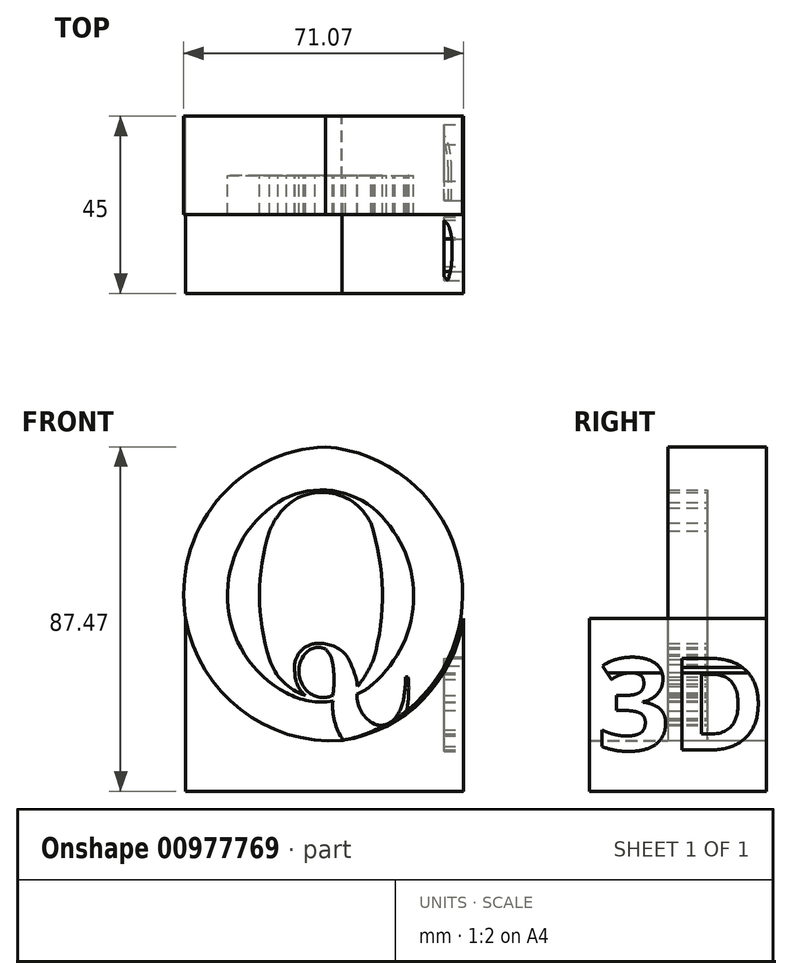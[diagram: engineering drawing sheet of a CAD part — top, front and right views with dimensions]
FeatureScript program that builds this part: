
annotation { "Feature Type Name" : "Feature", "Feature Type Description" : "" }
export const myFeature = defineFeature(function(context is Context, id is Id, definition is map)
    precondition{}
    {
        {
            var Q0;
            Q0=qCreatedBy(makeId("Front.planeOp"),FACE);
            var sketch = newSketch(context, id + "F0", { "sketchPlane" : qUnion([Q0])});
            skPoint(sketch, "E0.first.point", {"position": v(-8.97, 42.4) * mm});
            skPoint(sketch, "E0.second.point", {"position": v(4.84, -31.38) * mm});
            skPoint(sketch, "E0.third.point", {"position": v(40.23, 13.72) * mm});
            skArc(sketch, "E1", {"start": v(0, 43.7) * mm, "mid": v(-36.34, 3.66) * mm, "end": v(4.84, -31.38) * mm});
            skArc(sketch, "E2", {"start": v(20.57, -24) * mm, "mid": v(33.91, 17.02) * mm, "end": v(0, 43.7) * mm});
            skArc(sketch, "E3", {"start": v(-12, 29.47) * mm, "mid": v(-24.84, 4.65) * mm, "end": v(-9.87, -18.96) * mm});
            skArc(sketch, "E4", {"start": v(12.09, 28.05) * mm, "mid": v(0.27, 32.56) * mm, "end": v(-12, 29.47) * mm});
            skArc(sketch, "E5", {"start": v(12.09, -16.68) * mm, "mid": v(22.4, 5.68) * mm, "end": v(12.09, 28.05) * mm});
            skArc(sketch, "E6", {"start": v(8.11, -19.25) * mm, "mid": v(10.22, -18.15) * mm, "end": v(12.09, -16.68) * mm});
            skArc(sketch, "E7", {"start": v(-9.87, -18.96) * mm, "mid": v(-4.16, -21) * mm, "end": v(1.9, -21.05) * mm});
            skArc(sketch, "E8", {"start": v(1.9, -21.05) * mm, "mid": v(2.44, -26.48) * mm, "end": v(4.84, -31.38) * mm});
            skArc(sketch, "E9", {"start": v(8.11, -19.25) * mm, "mid": v(9.16, -23.77) * mm, "end": v(12.57, -26.92) * mm});
            skArc(sketch, "E10", {"start": v(12.57, -26.92) * mm, "mid": v(15.38, -27) * mm, "end": v(17.7, -25.42) * mm});
            skArc(sketch, "E11", {"start": v(17.7, -25.42) * mm, "mid": v(19.27, -22.75) * mm, "end": v(19.99, -19.74) * mm});
            skArc(sketch, "E12", {"start": v(19.99, -19.74) * mm, "mid": v(20.3, -17.3) * mm, "end": v(20.33, -14.85) * mm});
            skLineSegment(sketch, "E13", {"start": v(20.33, -14.85) * mm, "end": v(21.05, -14.85) * mm});
            skArc(sketch, "E14", {"start": v(20.57, -24) * mm, "mid": v(21.16, -19.45) * mm, "end": v(21.05, -14.85) * mm});
            skArc(sketch, "E15", {"start": v(11.56, 24.17) * mm, "mid": v(0.05, 31.98) * mm, "end": v(-12.33, 25.65) * mm});
            skArc(sketch, "E16", {"start": v(-12.33, 25.65) * mm, "mid": v(-13.33, 23.93) * mm, "end": v(-14.2, 22.14) * mm});
            skArc(sketch, "E17", {"start": v(12.27, -10.4) * mm, "mid": v(14.51, 6.94) * mm, "end": v(11.56, 24.17) * mm});
            skArc(sketch, "E18", {"start": v(8.2, -17.28) * mm, "mid": v(10.48, -13.99) * mm, "end": v(12.27, -10.4) * mm});
            skArc(sketch, "E19", {"start": v(-14.2, 22.14) * mm, "mid": v(-16.74, 5.87) * mm, "end": v(-14.2, -10.4) * mm});
            skArc(sketch, "E20", {"start": v(-14.2, -10.4) * mm, "mid": v(-10.74, -16.1) * mm, "end": v(-5.08, -19.62) * mm});
            skArc(sketch, "E21.trimOffspring", {"start": v(21.12, -15.68) * mm, "mid": v(21.07, -15.26) * mm, "end": v(21.03, -14.85) * mm});
            skArc(sketch, "E22", {"start": v(-7.75, -13.7) * mm, "mid": v(-7.09, -16.96) * mm, "end": v(-5.08, -19.62) * mm});
            skArc(sketch, "E23", {"start": v(-2.67, -6.43) * mm, "mid": v(-6.77, -8.98) * mm, "end": v(-7.75, -13.7) * mm});
            skArc(sketch, "E24", {"start": v(5.17, -9.2) * mm, "mid": v(1.57, -6.89) * mm, "end": v(-2.67, -6.43) * mm});
            skArc(sketch, "E25", {"start": v(8.2, -17.28) * mm, "mid": v(7.13, -13.07) * mm, "end": v(5.17, -9.2) * mm});
            skArc(sketch, "E26", {"start": v(1.9, -19.62) * mm, "mid": v(2.22, -15.67) * mm, "end": v(1.9, -11.72) * mm});
            skArc(sketch, "E27", {"start": v(1.9, -11.72) * mm, "mid": v(1.3, -9.59) * mm, "end": v(0, -7.8) * mm});
            skArc(sketch, "E28", {"start": v(0, -7.8) * mm, "mid": v(-3.12, -7.64) * mm, "end": v(-5.56, -9.59) * mm});
            skPoint(sketch, "E28.endSnap0", {"position": v(1.3, -9.59) * mm});
            skArc(sketch, "E29", {"start": v(-5.56, -9.59) * mm, "mid": v(-6.65, -14.33) * mm, "end": v(-4.4, -18.65) * mm});
            skArc(sketch, "E30", {"start": v(-4.4, -18.65) * mm, "mid": v(-1.39, -20.08) * mm, "end": v(1.9, -19.62) * mm});
            skSolve(sketch);
        }
        {
            var Q0;
            Q0=qSketchRegion(id+"F0",true);
            extrude(context, id + "F1", {"entities" : qUnion([Q0]), "depth" : 25 * mm, "offsetDistance" : 25 * mm});
        }
        {
            var Q0;
            Q0=makeQuery(id+"F1.opExtrude","CAP_FACE",FACE,{"disambiguationData":[OSD([sQuery(id+"F0.wireOp",EDGE,"E1"),sQuery(id+"F0.wireOp",EDGE,"E2"),sQuery(id+"F0.wireOp",EDGE,"E3"),sQuery(id+"F0.wireOp",EDGE,"E4"),sQuery(id+"F0.wireOp",EDGE,"E5"),sQuery(id+"F0.wireOp",EDGE,"E6"),sQuery(id+"F0.wireOp",EDGE,"E7"),sQuery(id+"F0.wireOp",EDGE,"E8"),sQuery(id+"F0.wireOp",EDGE,"E9"),sQuery(id+"F0.wireOp",EDGE,"E10"),sQuery(id+"F0.wireOp",EDGE,"E11"),sQuery(id+"F0.wireOp",EDGE,"E12"),sQuery(id+"F0.wireOp",EDGE,"E13"),sQuery(id+"F0.wireOp",EDGE,"E14"),sQuery(id+"F0.wireOp",EDGE,"E21.trimOffspring")])],"isStart":true});
            var sketch = newSketch(context, id + "F2", { "sketchPlane" : qUnion([Q0])});
            skArc(sketch, "E31", {"start": v(0, 43.7) * mm, "mid": v(-35.47, 8.29) * mm, "end": v(-4.84, -31.38) * mm});
            skArc(sketch, "E32", {"start": v(-4.84, -31.38) * mm, "mid": v(36.41, 3.65) * mm, "end": v(0, 43.7) * mm});
            skSolve(sketch);
        }
        {
            var Q0;
            Q0=qCreatedBy(makeId("Front.planeOp"),FACE);
            var sketch = newSketch(context, id + "F3", { "sketchPlane" : qUnion([Q0])});
            skArc(sketch, "E33", {"start": v(0, 43.75) * mm, "mid": v(-36.28, 3.67) * mm, "end": v(4.78, -31.5) * mm});
            skArc(sketch, "E34", {"start": v(4.78, -31.5) * mm, "mid": v(35.24, 8.21) * mm, "end": v(0, 43.75) * mm});
            skSolve(sketch);
        }
        {
            var Q0;
            Q0=qSketchRegion(id+"F3",true);
            extrude(context, id + "F4", {"entities" : qUnion([Q0]), "operationType" : NewBodyOperationType.ADD, "depth" : 10 * mm, "offsetDistance" : 25 * mm});
        }
        {
            var Q0;
            Q0=qSketchRegion(id+"F3",true);
            extrude(context, id + "F5", {"entities" : qUnion([Q0]), "operationType" : NewBodyOperationType.ADD, "depth" : 15 * mm, "offsetDistance" : 25 * mm});
        }
        {
            var Q0;
            Q0=makeQuery(id+"F2.imprint","IMPRINT",FACE,{"disambiguationData":[TD([[makeQuery(id+"F2.imprint","IMPRINT",EDGE,{"derivedFrom":makeQuery(id+"F1.opExtrude","CAP_EDGE",EDGE,{"disambiguationData":[OSD([sQuery(id+"F0.wireOp",EDGE,"E3")])],"isStart":true})}),-1.0]])]});
            var sketch = newSketch(context, id + "F6", { "sketchPlane" : qUnion([Q0])});
            skArc(sketch, "E35", {"start": v(0, 43.54) * mm, "mid": v(-34.85, 7.94) * mm, "end": v(-3.9, -31.1) * mm});
            skArc(sketch, "E36", {"start": v(-3.9, -31.1) * mm, "mid": v(35.93, 4.24) * mm, "end": v(0, 43.54) * mm});
            skSolve(sketch);
        }
        {
            var Q0;
            Q0=qSketchRegion(id+"F6",true);
            extrude(context, id + "F7", {"entities" : qUnion([Q0]), "operationType" : NewBodyOperationType.INTERSECT, "oppositeDirection" : true, "depth" : 109 * mm, "offsetDistance" : 25 * mm});
        }
        {
            var Q0;
            {var subQ2=makeQuery(id+"F1.opExtrude","CAP_EDGE",EDGE,{"disambiguationData":[OSD([sQuery(id+"F0.wireOp",EDGE,"E1")])],"isStart":true});Q0=makeQuery(id+"F2.imprint","IMPRINT",FACE,{"disambiguationData":[TD([[makeQuery(id+"F2.imprint","IMPRINT",EDGE,{"derivedFrom":subQ2}),-1.0]])]});}
            var sketch = newSketch(context, id + "F8", { "sketchPlane" : qUnion([Q0])});
            skLineSegment(sketch, "E37", {"start": v(-35.1, 0) * mm, "end": v(-35.1, -43.93) * mm});
            skLineSegment(sketch, "E38", {"start": v(-35.1, -43.93) * mm, "end": v(35.46, -43.93) * mm});
            skLineSegment(sketch, "E39", {"start": v(35.46, -43.93) * mm, "end": v(35.46, 0) * mm});
            skArc(sketch, "E40", {"start": v(-35.1, 0) * mm, "mid": v(-24.84, -20.62) * mm, "end": v(-4.3, -31.04) * mm});
            skArc(sketch, "E41", {"start": v(-4.3, -31.04) * mm, "mid": v(21.56, -23.18) * mm, "end": v(35.46, 0) * mm});
            skSolve(sketch);
        }
        {
            var Q0;
            Q0 = qSketchRegion(id + "F8", true);
            extrude(context, id + "F9", {"entities" : qUnion([Q0]), "operationType" : NewBodyOperationType.ADD, "oppositeDirection" : true, "depth" : 45 * mm, "offsetDistance" : 25 * mm});
        }
        {
            var Q0;
            Q0=makeQuery(id+"F9.opExtrude","SWEPT_FACE",FACE,{"disambiguationData":[OSD([sQuery(id+"F8.wireOp",EDGE,"E37")])]});
            var sketch = newSketch(context, id + "F10", { "sketchPlane" : qUnion([Q0])});
            skText(sketch, "E42", { "text": "3D", "fontName": "OpenSans-Bold.ttf"});
            const initialGuessF10  = {"E42": [-0.043, -0.0335, 1, 0, 0.0235]};
            skSetInitialGuess(sketch, initialGuessF10);
            skSolve(sketch);
        }
        {
            var Q0;
            Q0 = qSketchRegion(id + "F10", true);
            extrude(context, id + "F11", {"entities" : qUnion([Q0]), "operationType" : NewBodyOperationType.REMOVE, "oppositeDirection" : true, "depth" : 5 * mm, "offsetDistance" : 25 * mm});
        }
    });
